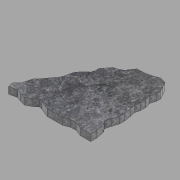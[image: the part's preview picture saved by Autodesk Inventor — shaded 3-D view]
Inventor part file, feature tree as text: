
AUTODESK INVENTOR PART (.ipt)
format: ipt  version: 2022.2 (Build 262287000, 287)  size: 161,280 bytes
history: native  units: in
note: dims shown in document units (in); Inventor stores cm internally (conversion verified against a paired STEP export)
features: extrude x1, sketch x1
ambient origin geometry x8: Origin, YZ Plane, XZ Plane, XY Plane, X Axis, Y Axis, Z Axis, Center Point
bodies: Solid1 (feature_tree)
feature tree (2):
  extrude  "Extrusion1"  [1 undecoded]
  sketch  "Sketch2"  dims[d2=1.0in d3=0.0in]
note: 1 required parameter value undecoded (feature->parameter linkage not recoverable at this tier; creation-order binding heuristic only, values carry confidence <= 0.55)
